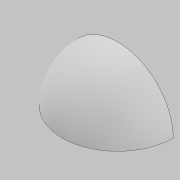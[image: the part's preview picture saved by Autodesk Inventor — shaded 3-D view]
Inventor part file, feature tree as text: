
AUTODESK INVENTOR PART (.ipt)
format: ipt  version: 2021 (Build 250183000, 183)  size: 120,320 bytes
history: native  units: mm
features: other x3, revolve x1, sketch x1
ambient origin geometry x8: Origin, YZ Plane, XZ Plane, XY Plane, X Axis, Y Axis, Z Axis, Center Point
bodies: Body1 (feature_tree)
feature tree (5):
  revolve  "Revolution1"  [1 undecoded]
  other  "midPlane"
  sketch  "Sketch1"  dims[d0=10.0mm d1=1000.0mm d2=0.0mm d3=0.0mm d6=180.0deg d9=0.872665mm d10=0.872665mm]
  other  "tangentPlane1"
  other  "tangentPlane2"
note: 1 required parameter value undecoded (feature->parameter linkage not recoverable at this tier; creation-order binding heuristic only, values carry confidence <= 0.55)
